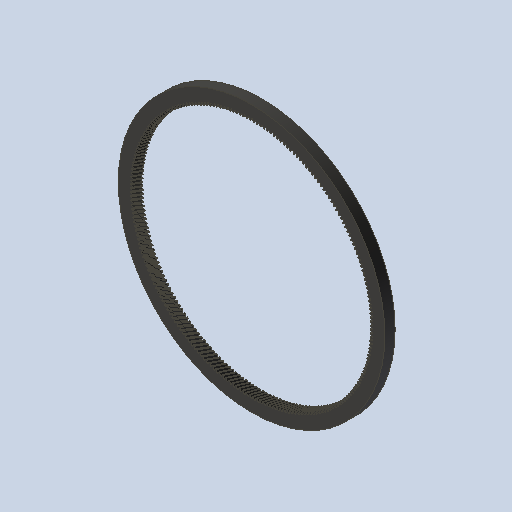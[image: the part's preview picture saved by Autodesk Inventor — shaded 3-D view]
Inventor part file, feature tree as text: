
AUTODESK INVENTOR PART (.ipt)
format: ipt  version: 2023 (Build 270158000, 158)  size: 2,451,968 bytes
history: native  units: mm (DEFAULTED — no unit token found)
features: plane x3, other x3, sketch x2, extrude x1
ambient origin geometry x8: Origin, YZ Plane, XZ Plane, XY Plane, X Axis, Y Axis, Z Axis, Center Point
bodies: Solid1 (feature_tree)
feature tree (9):
  extrude  "Extrusion1"  Depth=15.0mm TaperAngle=0.0deg
  plane  "Work Plane2"
  plane  "Work Plane8"
  plane  "Work Plane9"
  other  "Spur Gear"
  sketch  "Sketch1"  dims[d0=390.947114mm d1=15.0mm d2=0.0mm]
  sketch  "Sketch2"  dims[d3=351.178665mm d4=10.0mm d5=0.0mm d16=101.6mm d17=0.0mm d34=0.1428mm d39=0.0mm d45=0.0mm d47=101.6mm d50=0.0mm d51=0.0mm d52=101.6mm]
  other  "Srf1"
  other  "Pitch Diameter"
